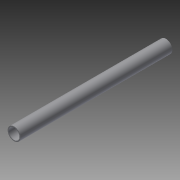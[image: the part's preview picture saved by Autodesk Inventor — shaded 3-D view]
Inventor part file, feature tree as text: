
AUTODESK INVENTOR PART (.ipt)
format: ipt  version: 2015 (Build 190159000, 159)  size: 72,704 bytes
history: native  units: in
note: dims shown in document units (in); Inventor stores cm internally (conversion verified against a paired STEP export)
features: extrude x1, sketch x1
ambient origin geometry x8: Origin, YZ Plane, XZ Plane, XY Plane, X Axis, Y Axis, Z Axis, Center Point
bodies: Solid1 (feature_tree)
feature tree (2):
  extrude  "Extrusion1"  Depth=28.0in
  sketch  "Sketch1"  dims[d0=2.0in d1=2.375in d2=28.0in d3=0.0in]
